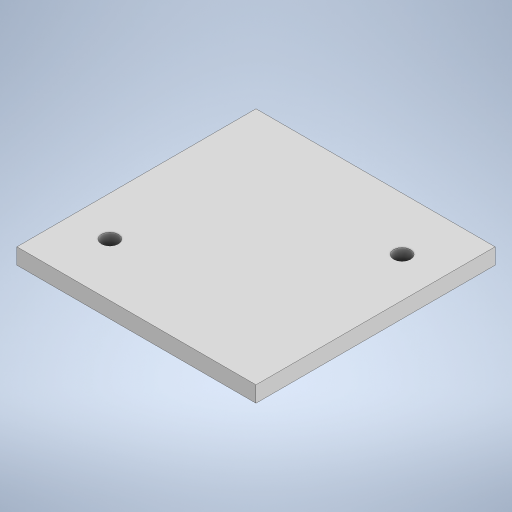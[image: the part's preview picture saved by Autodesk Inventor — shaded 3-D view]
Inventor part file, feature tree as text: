
AUTODESK INVENTOR PART (.ipt)
format: ipt  version: 2023 (Build 270158000, 158)  size: 211,968 bytes
history: native  units: mm
features: sketch x2, other x1, extrude x1, hole x1
ambient origin geometry x8: Origin, YZ Plane, XZ Plane, XY Plane, X Axis, Y Axis, Z Axis, Center Point
bodies: Body1 (feature_tree)
feature tree (5):
  other  "ソリッド1"
  extrude  "押し出し1"  Depth=45.0mm
  hole  "穴1"  [1 undecoded]
  sketch  "スケッチ1"
  sketch  "スケッチ2"
note: 1 required parameter value undecoded (feature->parameter linkage not recoverable at this tier; creation-order binding heuristic only, values carry confidence <= 0.55)
